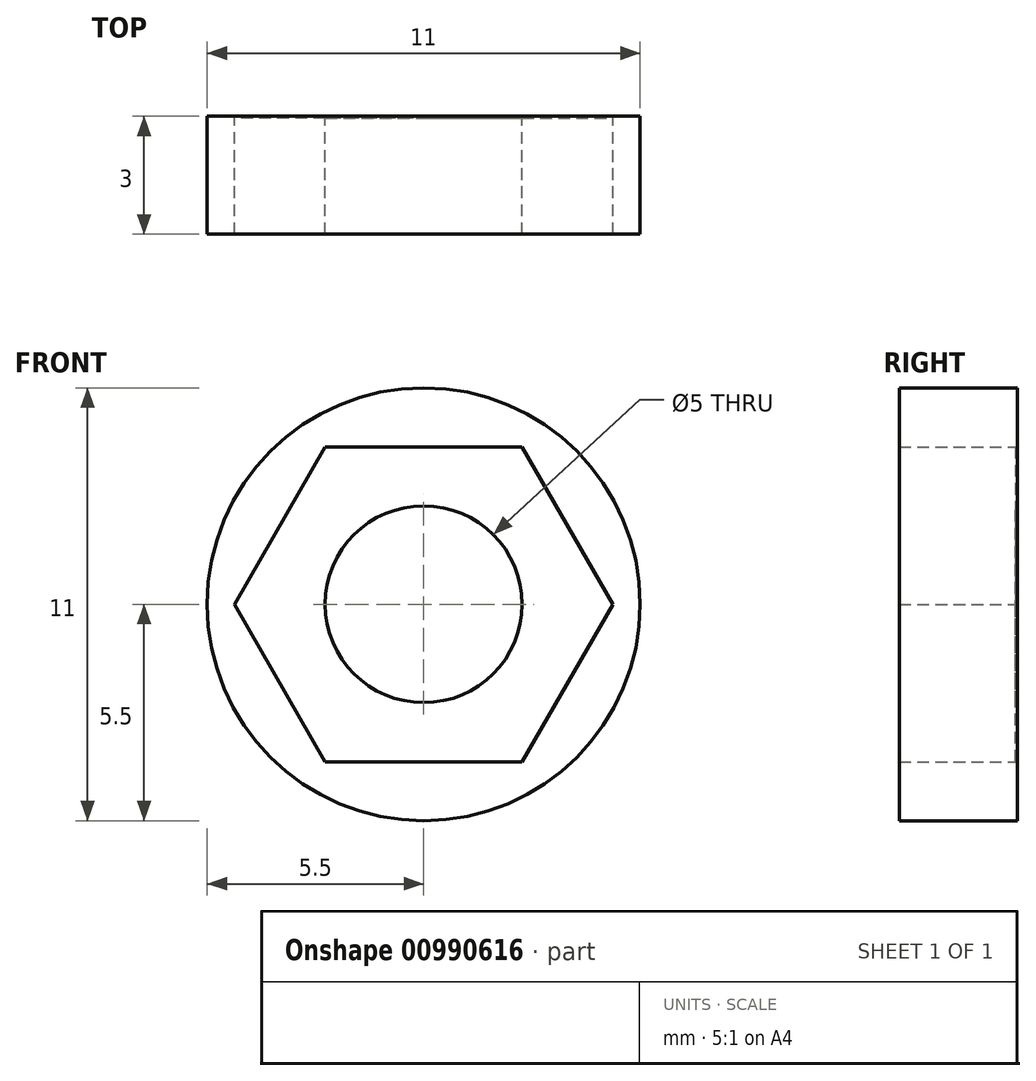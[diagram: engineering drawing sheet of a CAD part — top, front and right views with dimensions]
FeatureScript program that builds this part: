
annotation { "Feature Type Name" : "Feature", "Feature Type Description" : "" }
export const myFeature = defineFeature(function(context is Context, id is Id, definition is map)
    precondition{}
    {
        {
            var Q0;
            Q0=qCreatedBy(makeId("Front.planeOp"),FACE);
            var sketch = newSketch(context, id + "F0", { "sketchPlane" : qUnion([Q0])});
            skCircle(sketch, "E0", {"center": v(0, 0) * mm, "radius": 5.5 * mm});
            skLineSegment(sketch, "E1.bottom", {"start": v(-2.5, -4) * mm, "end": v(2.5, -4) * mm});
            skLineSegment(sketch, "E1.top", {"start": v(-2.5, 4) * mm, "end": v(2.5, 4) * mm});
            skLineSegment(sketch, "E1.left", {"start": v(-2.5, -4) * mm, "end": v(-2.5, 4) * mm});
            skLineSegment(sketch, "E1.right", {"start": v(2.5, -4) * mm, "end": v(2.5, 4) * mm});
            skLineSegment(sketch, "E2", {"start": v(-2.5, -4) * mm, "end": v(-4.8, 0) * mm});
            skLineSegment(sketch, "E3", {"start": v(-2.5, 4) * mm, "end": v(-4.8, 0) * mm});
            skLineSegment(sketch, "E4", {"start": v(2.5, 4) * mm, "end": v(4.8, 0) * mm});
            skLineSegment(sketch, "E5", {"start": v(4.8, 0) * mm, "end": v(2.5, -4) * mm});
            skSolve(sketch);
        }
        {
            var Q0;
            Q0 = qSketchRegion(id + "F0", true);
            extrude(context, id + "F1", {"entities" : qUnion([Q0]), "depth" : 3 * mm, "offsetDistance" : 25.4 * mm});
        }
        {
            var Q0;
            Q0=qCreatedBy(makeId("Front.planeOp"),FACE);
            var sketch = newSketch(context, id + "F2", { "sketchPlane" : qUnion([Q0])});
            skLineSegment(sketch, "E6.bottom", {"start": v(-3.38, -4.1) * mm, "end": v(3.38, -4.1) * mm});
            skLineSegment(sketch, "E6.top", {"start": v(-3.38, 4.1) * mm, "end": v(3.38, 4.1) * mm});
            skLineSegment(sketch, "E6.left", {"start": v(-3.38, -4.1) * mm, "end": v(-3.38, 4.1) * mm});
            skLineSegment(sketch, "E6.right", {"start": v(3.38, -4.1) * mm, "end": v(3.38, 4.1) * mm});
            skPoint(sketch, "E6.middle", {"position": v(0, 0) * mm});
            skLineSegment(sketch, "E7.bottom", {"start": v(-3.38, 2) * mm, "end": v(-4.51, 2) * mm});
            skLineSegment(sketch, "E7.top", {"start": v(-3.38, -1.86) * mm, "end": v(-4.51, -1.86) * mm});
            skLineSegment(sketch, "E7.left", {"start": v(-3.38, 2) * mm, "end": v(-3.38, -1.86) * mm});
            skLineSegment(sketch, "E7.right", {"start": v(-4.51, 2) * mm, "end": v(-4.51, -1.86) * mm});
            skLineSegment(sketch, "E8.bottom", {"start": v(-4.51, 0.87) * mm, "end": v(-5.1, 0.87) * mm});
            skLineSegment(sketch, "E8.top", {"start": v(-4.51, -0.87) * mm, "end": v(-5.1, -0.87) * mm});
            skLineSegment(sketch, "E8.left", {"start": v(-4.51, 0.87) * mm, "end": v(-4.51, -0.87) * mm});
            skLineSegment(sketch, "E8.right", {"start": v(-5.1, 0.87) * mm, "end": v(-5.1, -0.87) * mm});
            skLineSegment(sketch, "E9.bottom", {"start": v(3.38, 2.34) * mm, "end": v(4.44, 2.34) * mm});
            skLineSegment(sketch, "E9.top", {"start": v(3.38, -2.17) * mm, "end": v(4.44, -2.17) * mm});
            skLineSegment(sketch, "E9.left", {"start": v(3.38, 2.34) * mm, "end": v(3.38, -2.17) * mm});
            skLineSegment(sketch, "E9.right", {"start": v(4.44, 2.34) * mm, "end": v(4.44, -2.17) * mm});
            skLineSegment(sketch, "E10.bottom", {"start": v(4.44, 1.04) * mm, "end": v(5, 1.04) * mm});
            skLineSegment(sketch, "E10.top", {"start": v(4.44, -0.87) * mm, "end": v(5, -0.87) * mm});
            skLineSegment(sketch, "E10.left", {"start": v(4.44, 1.04) * mm, "end": v(4.44, -0.87) * mm});
            skLineSegment(sketch, "E10.right", {"start": v(5, 1.04) * mm, "end": v(5, -0.87) * mm});
            skCircle(sketch, "E11", {"center": v(0, 0) * mm, "radius": 2.5 * mm});
            skLineSegment(sketch, "E12.bottom", {"start": v(-3.38, -1.86) * mm, "end": v(-4.14, -1.86) * mm});
            skLineSegment(sketch, "E12.top", {"start": v(-3.38, -2.57) * mm, "end": v(-4.14, -2.57) * mm});
            skLineSegment(sketch, "E12.left", {"start": v(-3.38, -1.86) * mm, "end": v(-3.38, -2.57) * mm});
            skLineSegment(sketch, "E12.right", {"start": v(-4.14, -1.86) * mm, "end": v(-4.14, -2.57) * mm});
            skPoint(sketch, "E13.oppositeSnap0", {"position": v(3.91, -2.17) * mm});
            skLineSegment(sketch, "E13.bottom", {"start": v(3.38, -2.17) * mm, "end": v(3.91, -2.17) * mm});
            skLineSegment(sketch, "E13.top", {"start": v(3.38, -2.75) * mm, "end": v(3.91, -2.75) * mm});
            skLineSegment(sketch, "E13.left", {"start": v(3.38, -2.17) * mm, "end": v(3.38, -2.75) * mm});
            skLineSegment(sketch, "E13.right", {"start": v(3.91, -2.17) * mm, "end": v(3.91, -2.75) * mm});
            skLineSegment(sketch, "E14.bottom", {"start": v(3.38, 2.34) * mm, "end": v(3.78, 2.34) * mm});
            skLineSegment(sketch, "E14.top", {"start": v(3.38, 2.9) * mm, "end": v(3.78, 2.9) * mm});
            skLineSegment(sketch, "E14.left", {"start": v(3.38, 2.34) * mm, "end": v(3.38, 2.9) * mm});
            skLineSegment(sketch, "E14.right", {"start": v(3.78, 2.34) * mm, "end": v(3.78, 2.9) * mm});
            skLineSegment(sketch, "E15.bottom", {"start": v(-3.38, 2) * mm, "end": v(-4.03, 2) * mm});
            skLineSegment(sketch, "E15.top", {"start": v(-3.38, 2.71) * mm, "end": v(-4.03, 2.71) * mm});
            skLineSegment(sketch, "E15.left", {"start": v(-3.38, 2) * mm, "end": v(-3.38, 2.71) * mm});
            skLineSegment(sketch, "E15.right", {"start": v(-4.03, 2) * mm, "end": v(-4.03, 2.71) * mm});
            skSolve(sketch);
        }
        {
            var Q0;
            Q0 = qSketchRegion(id + "F2", true);
            extrude(context, id + "F3", {"entities" : qUnion([Q0]), "operationType" : NewBodyOperationType.ADD, "depth" : 0.05 * mm, "offsetDistance" : 25.4 * mm});
        }
    });
